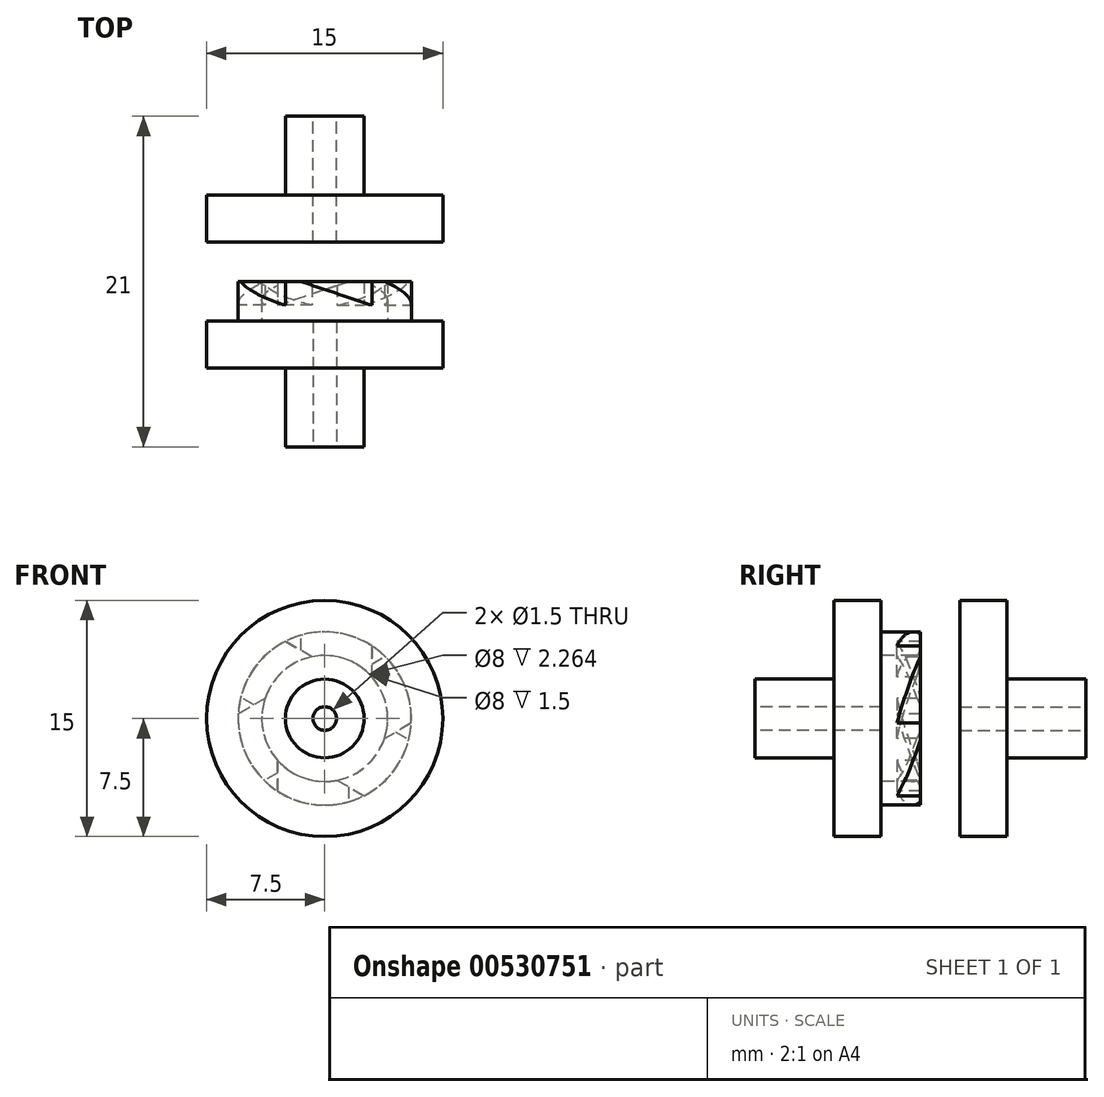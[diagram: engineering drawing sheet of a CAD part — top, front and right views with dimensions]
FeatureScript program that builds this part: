
annotation { "Feature Type Name" : "Feature", "Feature Type Description" : "" }
export const myFeature = defineFeature(function(context is Context, id is Id, definition is map)
    precondition{}
    {
        {
            var Q0;
            Q0=qCreatedBy(makeId("Front.planeOp"),FACE);
            var sketch = newSketch(context, id + "F0", { "sketchPlane" : qUnion([Q0])});
            skCircle(sketch, "E0", {"center": v(0, 0) * mm, "radius": 7.5 * mm});
            skSolve(sketch);
        }
        {
            var Q0;
            Q0 = qSketchRegion(id + "F0", true);
            extrude(context, id + "F1", {"entities" : qUnion([Q0]), "depth" : 3 * mm, "offsetDistance" : 25 * mm});
        }
        {
            var Q0;
            Q0=makeQuery(id+"F1.opExtrude","CAP_FACE",FACE,{"disambiguationData":[OSD([sQuery(id+"F0.wireOp",EDGE,"E0")])],"isStart":false});
            var sketch = newSketch(context, id + "F2", { "sketchPlane" : qUnion([Q0])});
            skCircle(sketch, "E1", {"center": v(0, 0) * mm, "radius": 2.5 * mm});
            skSolve(sketch);
        }
        {
            var Q0;
            Q0 = qSketchRegion(id + "F2", true);
            extrude(context, id + "F3", {"entities" : qUnion([Q0]), "operationType" : NewBodyOperationType.ADD, "depth" : 5 * mm, "offsetDistance" : 25 * mm});
        }
        {
            var Q0;
            Q0=makeQuery(id+"F3.opExtrude","CAP_FACE",FACE,{"disambiguationData":[OSD([sQuery(id+"F2.wireOp",EDGE,"E1")])],"isStart":false});
            var sketch = newSketch(context, id + "F4", { "sketchPlane" : qUnion([Q0])});
            skCircle(sketch, "E2", {"center": v(0, 0) * mm, "radius": 0.75 * mm});
            skSolve(sketch);
        }
        {
            var Q0;
            Q0 = qSketchRegion(id + "F4", true);
            extrude(context, id + "F5", {"entities" : qUnion([Q0]), "operationType" : NewBodyOperationType.REMOVE, "endBound" : BoundingType.THROUGH_ALL, "oppositeDirection" : true, "depth" : 25 * mm, "offsetDistance" : 25 * mm});
        }
        {
            var Q0;
            Q0=makeQuery(id+"F1.opExtrude","CAP_FACE",FACE,{"disambiguationData":[OSD([sQuery(id+"F0.wireOp",EDGE,"E0")])],"isStart":false});
            var sketch = newSketch(context, id + "F6", { "sketchPlane" : qUnion([Q0])});
            skCircle(sketch, "E3", {"center": v(0, 0) * mm, "radius": 5.5 * mm});
            skCircle(sketch, "E4", {"center": v(0, 0) * mm, "radius": 4 * mm});
            skSolve(sketch);
        }
        {
            var Q0;
            Q0=makeQuery(id+"F6.imprint","IMPRINT",FACE,{"disambiguationData":[TD([[makeQuery(id+"F6.imprint","IMPRINT",EDGE,{"derivedFrom":sQuery(id+"F6.wireOp",EDGE,"E3")}),1.0]])]});
            extrude(context, id + "F7", {"entities" : qUnion([Q0]), "operationType" : NewBodyOperationType.ADD, "oppositeDirection" : true, "depth" : 6 * mm, "offsetDistance" : 25 * mm});
        }
        {
            var Q0;
            Q0=qCreatedBy(makeId("Top.planeOp"),FACE);
            cPlane(context, id + "F8", {"entities" : qUnion([Q0]), "cplaneType" : CPlaneType.OFFSET, "offset" : 10 * mm, "width" : 150 * mm, "height" : 150 * mm});
        }
        {
            var Q0;
            Q0=qCreatedBy(id+"F8.planeOp",FACE);
            var sketch = newSketch(context, id + "F9", { "sketchPlane" : qUnion([Q0])});
            skLineSegment(sketch, "E5", {"start": v(3, 1) * mm, "end": v(3, 3) * mm});
            skLineSegment(sketch, "E6", {"start": v(3, 3) * mm, "end": v(-3, 3) * mm});
            skPoint(sketch, "E7", {"position": v(0, 3) * mm});
            skLineSegment(sketch, "E8", {"start": v(-3, 3) * mm, "end": v(3, 1) * mm});
            skSolve(sketch);
        }
        {
            var Q0;
            Q0 = qSketchRegion(id + "F9", true);
            extrude(context, id + "F10", {"entities" : qUnion([Q0]), "oppositeDirection" : true, "depth" : 10 * mm, "offsetDistance" : 25 * mm});
        }
        {
            var Q0;
            Q0=makeQuery(id+"F10.opExtrude","SWEPT_BODY",BODY,{"disambiguationData":[OSD([sQuery(id+"F9.wireOp",EDGE,"E5"),sQuery(id+"F9.wireOp",EDGE,"E6"),sQuery(id+"F9.wireOp",EDGE,"E8")])]});
            var Q1;
            Q1=makeQuery(id+"F7.opExtrude","CAP_EDGE",EDGE,{"disambiguationData":[OSD([sQuery(id+"F6.wireOp",EDGE,"E4")])],"isStart":false});
            circularPattern(context, id + "F11", {"entities" : qUnion([Q0]), "axis" : qUnion([Q1]), "angle" : 360 * degree, "instanceCount" : 6, "equalSpace" : true, "computeTransformsWithoutBuiltin" : true});
        }
        {
            var Q0;
            Q0=makeQuery(id+"F11.opPattern","COPY",BODY,{"derivedFrom":makeQuery(id+"F10.opExtrude","SWEPT_BODY",BODY,{"disambiguationData":[OSD([sQuery(id+"F9.wireOp",EDGE,"E5"),sQuery(id+"F9.wireOp",EDGE,"E6"),sQuery(id+"F9.wireOp",EDGE,"E8")])]}),"instanceName":"3"});
            var Q1;
            Q1=makeQuery(id+"F11.opPattern","COPY",BODY,{"derivedFrom":makeQuery(id+"F10.opExtrude","SWEPT_BODY",BODY,{"disambiguationData":[OSD([sQuery(id+"F9.wireOp",EDGE,"E5"),sQuery(id+"F9.wireOp",EDGE,"E6"),sQuery(id+"F9.wireOp",EDGE,"E8")])]}),"instanceName":"6"});
            var Q2;
            Q2=makeQuery(id+"F11.opPattern","COPY",BODY,{"derivedFrom":makeQuery(id+"F10.opExtrude","SWEPT_BODY",BODY,{"disambiguationData":[OSD([sQuery(id+"F9.wireOp",EDGE,"E5"),sQuery(id+"F9.wireOp",EDGE,"E6"),sQuery(id+"F9.wireOp",EDGE,"E8")])]}),"instanceName":"4"});
            var Q3;
            Q3=makeQuery(id+"F11.opPattern","COPY",BODY,{"derivedFrom":makeQuery(id+"F10.opExtrude","SWEPT_BODY",BODY,{"disambiguationData":[OSD([sQuery(id+"F9.wireOp",EDGE,"E5"),sQuery(id+"F9.wireOp",EDGE,"E6"),sQuery(id+"F9.wireOp",EDGE,"E8")])]}),"instanceName":"5"});
            var Q4;
            Q4=makeQuery(id+"F10.opExtrude","SWEPT_BODY",BODY,{"disambiguationData":[OSD([sQuery(id+"F9.wireOp",EDGE,"E5"),sQuery(id+"F9.wireOp",EDGE,"E6"),sQuery(id+"F9.wireOp",EDGE,"E8")])]});
            var Q5;
            Q5=makeQuery(id+"F11.opPattern","COPY",BODY,{"derivedFrom":makeQuery(id+"F10.opExtrude","SWEPT_BODY",BODY,{"disambiguationData":[OSD([sQuery(id+"F9.wireOp",EDGE,"E5"),sQuery(id+"F9.wireOp",EDGE,"E6"),sQuery(id+"F9.wireOp",EDGE,"E8")])]}),"instanceName":"7"});
            var Q6;
            Q6=makeQuery(id+"F11.opPattern","COPY",BODY,{"derivedFrom":makeQuery(id+"F10.opExtrude","SWEPT_BODY",BODY,{"disambiguationData":[OSD([sQuery(id+"F9.wireOp",EDGE,"E5"),sQuery(id+"F9.wireOp",EDGE,"E6"),sQuery(id+"F9.wireOp",EDGE,"E8")])]}),"instanceName":"1"});
            var Q7;
            Q7=makeQuery(id+"F11.opPattern","COPY",BODY,{"derivedFrom":makeQuery(id+"F10.opExtrude","SWEPT_BODY",BODY,{"disambiguationData":[OSD([sQuery(id+"F9.wireOp",EDGE,"E5"),sQuery(id+"F9.wireOp",EDGE,"E6"),sQuery(id+"F9.wireOp",EDGE,"E8")])]}),"instanceName":"8"});
            var Q8;
            Q8=makeQuery(id+"F11.opPattern","COPY",BODY,{"derivedFrom":makeQuery(id+"F10.opExtrude","SWEPT_BODY",BODY,{"disambiguationData":[OSD([sQuery(id+"F9.wireOp",EDGE,"E5"),sQuery(id+"F9.wireOp",EDGE,"E6"),sQuery(id+"F9.wireOp",EDGE,"E8")])]}),"instanceName":"2"});
            var Q9;
            Q9=makeQuery(id+"F11.opPattern","COPY",BODY,{"derivedFrom":makeQuery(id+"F10.opExtrude","SWEPT_BODY",BODY,{"disambiguationData":[OSD([sQuery(id+"F9.wireOp",EDGE,"E5"),sQuery(id+"F9.wireOp",EDGE,"E6"),sQuery(id+"F9.wireOp",EDGE,"E8")])]}),"instanceName":"11"});
            var Q10;
            Q10=makeQuery(id+"F11.opPattern","COPY",BODY,{"derivedFrom":makeQuery(id+"F10.opExtrude","SWEPT_BODY",BODY,{"disambiguationData":[OSD([sQuery(id+"F9.wireOp",EDGE,"E5"),sQuery(id+"F9.wireOp",EDGE,"E6"),sQuery(id+"F9.wireOp",EDGE,"E8")])]}),"instanceName":"10"});
            var Q11;
            Q11=makeQuery(id+"F11.opPattern","COPY",BODY,{"derivedFrom":makeQuery(id+"F10.opExtrude","SWEPT_BODY",BODY,{"disambiguationData":[OSD([sQuery(id+"F9.wireOp",EDGE,"E5"),sQuery(id+"F9.wireOp",EDGE,"E6"),sQuery(id+"F9.wireOp",EDGE,"E8")])]}),"instanceName":"9"});
            var Q12;
            Q12=makeQuery(id+"F11.opPattern","COPY",BODY,{"derivedFrom":makeQuery(id+"F10.opExtrude","SWEPT_BODY",BODY,{"disambiguationData":[OSD([sQuery(id+"F9.wireOp",EDGE,"E5"),sQuery(id+"F9.wireOp",EDGE,"E6"),sQuery(id+"F9.wireOp",EDGE,"E8")])]}),"instanceName":"12"});
            var Q13;
            Q13=makeQuery(id+"F11.opPattern","COPY",BODY,{"derivedFrom":makeQuery(id+"F10.opExtrude","SWEPT_BODY",BODY,{"disambiguationData":[OSD([sQuery(id+"F9.wireOp",EDGE,"E5"),sQuery(id+"F9.wireOp",EDGE,"E6"),sQuery(id+"F9.wireOp",EDGE,"E8")])]}),"instanceName":"13"});
            var Q14;
            Q14=makeQuery(id+"F11.opPattern","COPY",BODY,{"derivedFrom":makeQuery(id+"F10.opExtrude","SWEPT_BODY",BODY,{"disambiguationData":[OSD([sQuery(id+"F9.wireOp",EDGE,"E5"),sQuery(id+"F9.wireOp",EDGE,"E6"),sQuery(id+"F9.wireOp",EDGE,"E8")])]}),"instanceName":"14"});
            var Q15;
            Q15=makeQuery(id+"F11.opPattern","COPY",BODY,{"derivedFrom":makeQuery(id+"F10.opExtrude","SWEPT_BODY",BODY,{"disambiguationData":[OSD([sQuery(id+"F9.wireOp",EDGE,"E5"),sQuery(id+"F9.wireOp",EDGE,"E6"),sQuery(id+"F9.wireOp",EDGE,"E8")])]}),"instanceName":"15"});
            var Q16;
            Q16=makeQuery(id+"F11.opPattern","COPY",BODY,{"derivedFrom":makeQuery(id+"F10.opExtrude","SWEPT_BODY",BODY,{"disambiguationData":[OSD([sQuery(id+"F9.wireOp",EDGE,"E5"),sQuery(id+"F9.wireOp",EDGE,"E6"),sQuery(id+"F9.wireOp",EDGE,"E8")])]}),"instanceName":"16"});
            var Q17;
            Q17=makeQuery(id+"F11.opPattern","COPY",BODY,{"derivedFrom":makeQuery(id+"F10.opExtrude","SWEPT_BODY",BODY,{"disambiguationData":[OSD([sQuery(id+"F9.wireOp",EDGE,"E5"),sQuery(id+"F9.wireOp",EDGE,"E6"),sQuery(id+"F9.wireOp",EDGE,"E8")])]}),"instanceName":"17"});
            var Q18;
            Q18=makeQuery(id+"F11.opPattern","COPY",BODY,{"derivedFrom":makeQuery(id+"F10.opExtrude","SWEPT_BODY",BODY,{"disambiguationData":[OSD([sQuery(id+"F9.wireOp",EDGE,"E5"),sQuery(id+"F9.wireOp",EDGE,"E6"),sQuery(id+"F9.wireOp",EDGE,"E8")])]}),"instanceName":"18"});
            var Q19;
            Q19=makeQuery(id+"F11.opPattern","COPY",BODY,{"derivedFrom":makeQuery(id+"F10.opExtrude","SWEPT_BODY",BODY,{"disambiguationData":[OSD([sQuery(id+"F9.wireOp",EDGE,"E5"),sQuery(id+"F9.wireOp",EDGE,"E6"),sQuery(id+"F9.wireOp",EDGE,"E8")])]}),"instanceName":"19"});
            var Q20;
            Q20=makeQuery(id+"F11.opPattern","COPY",BODY,{"derivedFrom":makeQuery(id+"F10.opExtrude","SWEPT_BODY",BODY,{"disambiguationData":[OSD([sQuery(id+"F9.wireOp",EDGE,"E5"),sQuery(id+"F9.wireOp",EDGE,"E6"),sQuery(id+"F9.wireOp",EDGE,"E8")])]}),"instanceName":"20"});
            var Q21;
            Q21=makeQuery(id+"F11.opPattern","COPY",BODY,{"derivedFrom":makeQuery(id+"F10.opExtrude","SWEPT_BODY",BODY,{"disambiguationData":[OSD([sQuery(id+"F9.wireOp",EDGE,"E5"),sQuery(id+"F9.wireOp",EDGE,"E6"),sQuery(id+"F9.wireOp",EDGE,"E8")])]}),"instanceName":"21"});
            var Q22;
            Q22=makeQuery(id+"F1.opExtrude","SWEPT_BODY",BODY,{"disambiguationData":[OSD([sQuery(id+"F0.wireOp",EDGE,"E0")])]});
            booleanBodies(context, id + "F12", {"operationType" : BooleanOperationType.SUBTRACTION, "tools" : qUnion([Q0, Q1, Q2, Q3, Q4, Q5, Q6, Q7, Q8, Q9, Q10, Q11, Q12, Q13, Q14, Q15, Q16, Q17, Q18, Q19, Q20, Q21]), "targets" : qUnion([Q22])});
        }
        {
            var Q0;
            {var subQ0=sQuery(id+"F0.wireOp",EDGE,"E0");Q0=makeQuery(id+"F7.boolean.opBoolean","SPLIT",FACE,{"disambiguationData":[TD([makeQuery(id+"F1.opExtrude","SWEPT_FACE",FACE,{"disambiguationData":[OSD([subQ0])]})])],"derivedFrom":makeQuery(id+"F1.opExtrude","CAP_FACE",FACE,{"disambiguationData":[OSD([subQ0])],"isStart":true})});}
            var sketch = newSketch(context, id + "F13", { "sketchPlane" : qUnion([Q0])});
            skCircle(sketch, "E9.0", {"center": v(0, 0) * mm, "radius": 5.5 * mm});
            skCircle(sketch, "E10.0", {"center": v(0, 0) * mm, "radius": 4 * mm});
            skSolve(sketch);
        }
        {
            var Q0;
            Q0 = qSketchRegion(id + "F13", true);
            extrude(context, id + "F14", {"entities" : qUnion([Q0]), "depth" : 5 * mm, "offsetDistance" : 25 * mm});
        }
        {
            var Q0;
            Q0=makeQuery(id+"F14.opExtrude","CAP_FACE",FACE,{"disambiguationData":[OSD([sQuery(id+"F13.wireOp",EDGE,"E9.0"),sQuery(id+"F13.wireOp",EDGE,"E10.0")])],"isStart":false});
            var sketch = newSketch(context, id + "F15", { "sketchPlane" : qUnion([Q0])});
            skCircle(sketch, "E11.0", {"center": v(0, 0) * mm, "radius": 7.5 * mm});
            skSolve(sketch);
        }
        {
            var Q0;
            Q0 = qSketchRegion(id + "F15", true);
            extrude(context, id + "F16", {"entities" : qUnion([Q0]), "operationType" : NewBodyOperationType.ADD, "depth" : 3 * mm, "offsetDistance" : 25 * mm});
        }
        {
            var Q0;
            Q0=makeQuery(id+"F16.opExtrude","CAP_FACE",FACE,{"disambiguationData":[OSD([sQuery(id+"F15.wireOp",EDGE,"E11.0")])],"isStart":false});
            var sketch = newSketch(context, id + "F17", { "sketchPlane" : qUnion([Q0])});
            skCircle(sketch, "E12.0", {"center": v(0, 0) * mm, "radius": 2.5 * mm});
            skSolve(sketch);
        }
        {
            var Q0;
            Q0 = qSketchRegion(id + "F17", true);
            extrude(context, id + "F18", {"entities" : qUnion([Q0]), "operationType" : NewBodyOperationType.ADD, "depth" : 5 * mm, "offsetDistance" : 25 * mm});
        }
        {
            var Q0;
            Q0=makeQuery(id+"F18.opExtrude","CAP_FACE",FACE,{"disambiguationData":[OSD([sQuery(id+"F17.wireOp",EDGE,"E12.0")])],"isStart":false});
            var sketch = newSketch(context, id + "F19", { "sketchPlane" : qUnion([Q0])});
            skCircle(sketch, "E13.0", {"center": v(0, 0) * mm, "radius": 0.75 * mm});
            skSolve(sketch);
        }
        {
            var Q0;
            Q0 = qSketchRegion(id + "F19", true);
            extrude(context, id + "F20", {"entities" : qUnion([Q0]), "operationType" : NewBodyOperationType.REMOVE, "oppositeDirection" : true, "depth" : 25 * mm, "offsetDistance" : 25 * mm});
        }
        {
            var Q0;
            Q0=makeQuery(id+"F1.opExtrude","SWEPT_BODY",BODY,{"disambiguationData":[OSD([sQuery(id+"F0.wireOp",EDGE,"E0")])]});
            var Q1;
            Q1=makeQuery(id+"F14.opExtrude","SWEPT_BODY",BODY,{"disambiguationData":[OSD([sQuery(id+"F13.wireOp",EDGE,"E9.0"),sQuery(id+"F13.wireOp",EDGE,"E10.0")])]});
            booleanBodies(context, id + "F21", {"operationType" : BooleanOperationType.SUBTRACTION, "tools" : qUnion([Q0]), "targets" : qUnion([Q1]), "keepTools" : true});
        }
        {
            var Q0;
            {var subQ0=sQuery(id+"F15.wireOp",EDGE,"E11.0");Q0=makeQuery(id+"F16.boolean.opBoolean","SPLIT",FACE,{"disambiguationData":[TD([makeQuery(id+"F14.opExtrude","SWEPT_FACE",FACE,{"disambiguationData":[OSD([sQuery(id+"F13.wireOp",EDGE,"E9.0")])]})])],"derivedFrom":makeQuery(id+"F16.opExtrude","CAP_FACE",FACE,{"disambiguationData":[OSD([subQ0])],"isStart":true})});}
            var sketch = newSketch(context, id + "F22", { "sketchPlane" : qUnion([Q0])});
            skCircle(sketch, "E14.0", {"center": v(0, 0) * mm, "radius": 7.5 * mm});
            skSolve(sketch);
        }
        {
            var Q0;
            Q0 = qSketchRegion(id + "F22", true);
            extrude(context, id + "F23", {"entities" : qUnion([Q0]), "operationType" : NewBodyOperationType.REMOVE, "depth" : 2.5 * mm, "offsetDistance" : 25 * mm});
        }
    });
